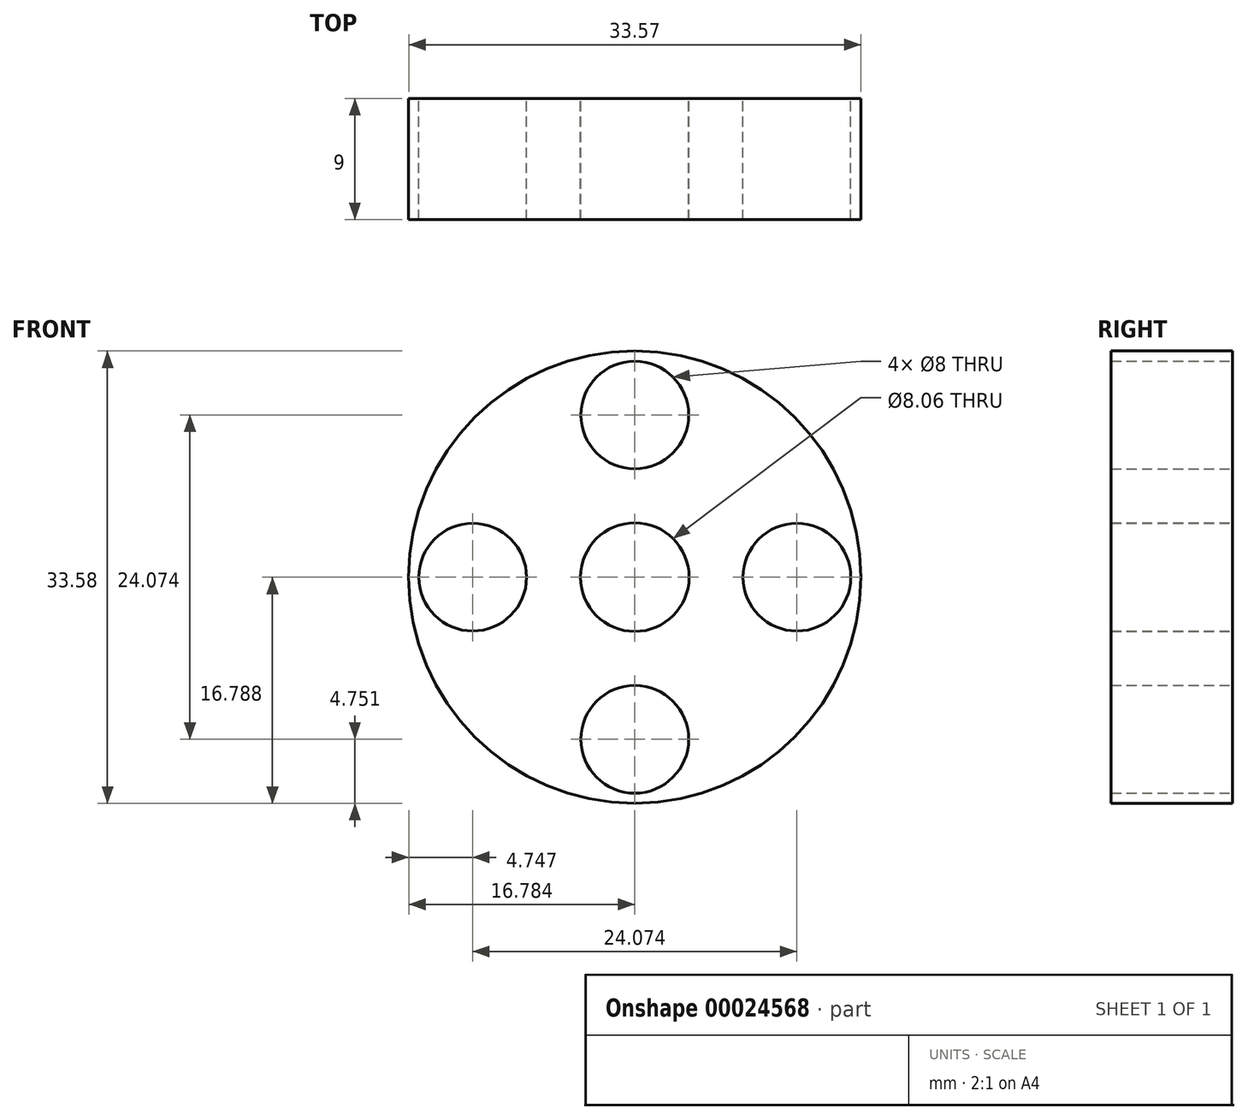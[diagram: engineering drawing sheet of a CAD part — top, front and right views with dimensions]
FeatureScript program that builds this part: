
annotation { "Feature Type Name" : "Feature", "Feature Type Description" : "" }
export const myFeature = defineFeature(function(context is Context, id is Id, definition is map)
    precondition{}
    {
        {
            var Q0;
            Q0=qCreatedBy(makeId("Front.planeOp"),FACE);
            var sketch = newSketch(context, id + "F0", { "sketchPlane" : qUnion([Q0])});
            skCircle(sketch, "E0", {"center": v(-19.96, 31.58) * mm, "radius": 7.5 * mm});
            skCircle(sketch, "E1", {"center": v(-19.96, 43.62) * mm, "radius": 4 * mm});
            skCircle(sketch, "E2.1.1", {"center": v(-32, 31.58) * mm, "radius": 4 * mm});
            skCircle(sketch, "E2.2.1", {"center": v(-19.96, 19.54) * mm, "radius": 4 * mm});
            skCircle(sketch, "E2.3.1", {"center": v(-7.92, 31.58) * mm, "radius": 4 * mm});
            skCircle(sketch, "E3", {"center": v(-19.96, 31.58) * mm, "radius": 16.79 * mm});
            skCircle(sketch, "E4", {"center": v(-19.96, 31.58) * mm, "radius": 4.03 * mm});
            skLineSegment(sketch, "E5", {"start": v(-19.96, 31.58) * mm, "end": v(-7.92, 43.28) * mm});
            skSolve(sketch);
        }
        {
            var Q0;
            Q0=makeQuery(id+"F0.imprint","IMPRINT",FACE,{"disambiguationData":[TD([[makeQuery(id+"F0.imprint","IMPRINT",EDGE,{"derivedFrom":sQuery(id+"F0.wireOp",EDGE,"E0")}),-1.0]])]});
            extrude(context, id + "F1", {"entities" : qUnion([Q0]), "depth" : 6 * mm});
        }
        {
            var Q0;
            Q0 = qSketchRegion(id + "F0", true);
            var Q1;
            Q1=makeQuery(id+"F0.imprint","IMPRINT",FACE,{"disambiguationData":[TD([[makeQuery(id+"F0.imprint","IMPRINT",EDGE,{"derivedFrom":sQuery(id+"F0.wireOp",EDGE,"E0")}),1.0]])]});
            extrude(context, id + "F2", {"entities" : qUnion([Q0, Q1]), "operationType" : NewBodyOperationType.ADD, "depth" : 9 * mm});
        }
    });
